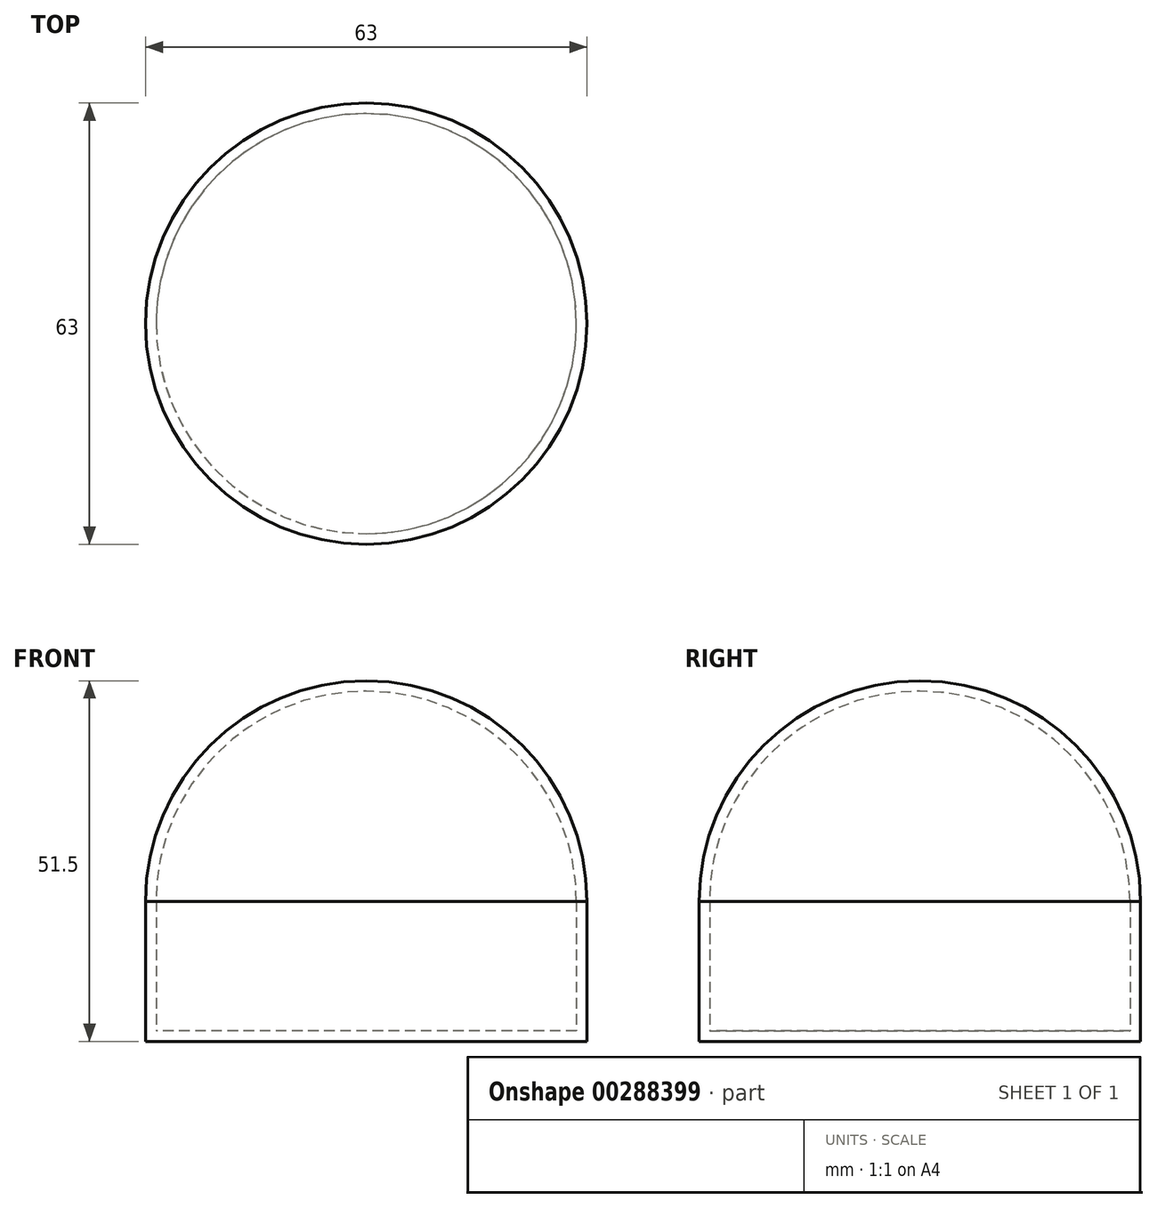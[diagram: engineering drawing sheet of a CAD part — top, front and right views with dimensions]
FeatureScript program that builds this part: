
annotation { "Feature Type Name" : "Feature", "Feature Type Description" : "" }
export const myFeature = defineFeature(function(context is Context, id is Id, definition is map)
    precondition{}
    {
        {
            var Q0;
            Q0=qCreatedBy(makeId("Top.planeOp"),FACE);
            var sketch = newSketch(context, id + "F0", { "sketchPlane" : qUnion([Q0])});
            skCircle(sketch, "E0", {"center": v(0, 0) * mm, "radius": 31.5 * mm});
            skSolve(sketch);
        }
        {
            var Q0;
            Q0=makeQuery(id+"F0.imprint","IMPRINT",FACE,{"disambiguationData":[TD([[makeQuery(id+"F0.imprint","IMPRINT",EDGE,{"derivedFrom":sQuery(id+"F0.wireOp",EDGE,"E0")}),1.0]])]});
            extrude(context, id + "F1", {"entities" : qUnion([Q0]), "depth" : 20 * mm});
        }
        {
            var Q0;
            Q0=qCreatedBy(makeId("Top.planeOp"),FACE);
            var sketch = newSketch(context, id + "F2", { "sketchPlane" : qUnion([Q0])});
            skCircle(sketch, "E1", {"center": v(0, 0) * mm, "radius": 30 * mm});
            skSolve(sketch);
        }
        {
            var Q0;
            Q0 = qSketchRegion(id + "F2", true);
            extrude(context, id + "F3", {"entities" : qUnion([Q0]), "depth" : 18.5 * mm});
        }
        {
            var Q0;
            Q0=makeQuery(id+"F3.opExtrude","SWEPT_BODY",BODY,{"disambiguationData":[OSD([sQuery(id+"F2.wireOp",EDGE,"E1")])]});
            transform(context, id + "F4", {"entities" : qUnion([Q0]), "transformType" : TransformType.TRANSLATION_3D, "dx" : 0 * mm, "dy" : 0 * mm, "dz" : 1.5 * mm, "makeCopy" : false});
        }
        {
            var Q0;
            Q0=makeQuery(id+"F3.opExtrude","SWEPT_BODY",BODY,{"disambiguationData":[OSD([sQuery(id+"F2.wireOp",EDGE,"E1")])]});
            var Q1;
            Q1=makeQuery(id+"F1.opExtrude","SWEPT_BODY",BODY,{"disambiguationData":[OSD([sQuery(id+"F0.wireOp",EDGE,"E0")])]});
            booleanBodies(context, id + "F5", {"operationType" : BooleanOperationType.SUBTRACTION, "tools" : qUnion([Q0]), "targets" : qUnion([Q1])});
        }
        {
            var Q0;
            Q0=qCreatedBy(makeId("Top.planeOp"),FACE);
            var sketch = newSketch(context, id + "F6", { "sketchPlane" : qUnion([Q0])});
            skArc(sketch, "E2", {"start": v(0, -31.5) * mm, "mid": v(31.5, 0) * mm, "end": v(0, 31.5) * mm});
            skLineSegment(sketch, "E3", {"start": v(0, 31.5) * mm, "end": v(0, -31.5) * mm});
            skSolve(sketch);
        }
        {
            var Q0;
            Q0 = qSketchRegion(id + "F6", true);
            var Q1;
            Q1=sQuery(id+"F6.wireOp",EDGE,"E3");
            revolve(context, id + "F7", {"entities" : qUnion([Q0]), "axis" : qUnion([Q1]), "revolveType" : RevolveType.ONE_DIRECTION, "angle" : 180 * degree});
        }
        {
            var Q0;
            Q0=qCreatedBy(makeId("Top.planeOp"),FACE);
            var sketch = newSketch(context, id + "F8", { "sketchPlane" : qUnion([Q0])});
            skArc(sketch, "E4", {"start": v(0, -30) * mm, "mid": v(30, 0) * mm, "end": v(0, 30) * mm});
            skLineSegment(sketch, "E5", {"start": v(0, 30) * mm, "end": v(0, -30) * mm});
            skSolve(sketch);
        }
        {
            var Q0;
            Q0 = qSketchRegion(id + "F8", true);
            var Q1;
            Q1=sQuery(id+"F8.wireOp",EDGE,"E5");
            revolve(context, id + "F9", {"entities" : qUnion([Q0]), "axis" : qUnion([Q1]), "revolveType" : RevolveType.ONE_DIRECTION, "angle" : 180 * degree});
        }
        {
            var Q0;
            Q0=makeQuery(id+"F9.opRevolve","SWEPT_BODY",BODY,{"disambiguationData":[OSD([sQuery(id+"F8.wireOp",EDGE,"E4"),sQuery(id+"F8.wireOp",EDGE,"E5")])]});
            var Q1;
            Q1=makeQuery(id+"F7.opRevolve","SWEPT_BODY",BODY,{"disambiguationData":[OSD([sQuery(id+"F6.wireOp",EDGE,"E2"),sQuery(id+"F6.wireOp",EDGE,"E3")])]});
            booleanBodies(context, id + "F10", {"operationType" : BooleanOperationType.SUBTRACTION, "tools" : qUnion([Q0]), "targets" : qUnion([Q1])});
        }
        {
            var Q0;
            Q0=makeQuery(id+"F7.opRevolve","SWEPT_BODY",BODY,{"disambiguationData":[OSD([sQuery(id+"F6.wireOp",EDGE,"E2"),sQuery(id+"F6.wireOp",EDGE,"E3")])]});
            transform(context, id + "F11", {"entities" : qUnion([Q0]), "transformType" : TransformType.TRANSLATION_3D, "dx" : 0 * mm, "dy" : 0 * mm, "dz" : 20 * mm, "makeCopy" : false});
        }
    });
